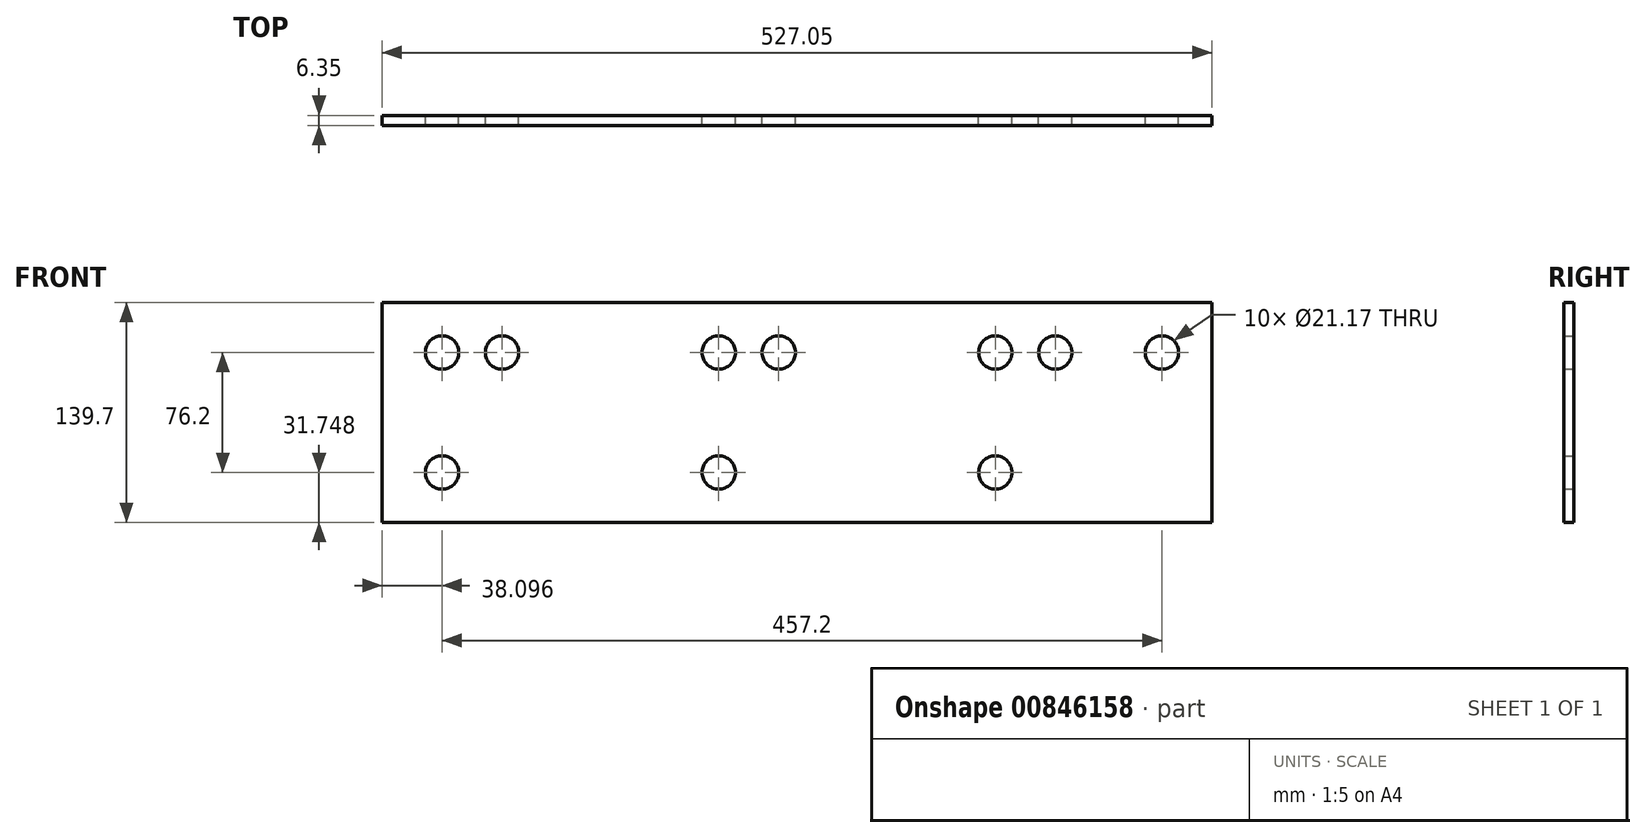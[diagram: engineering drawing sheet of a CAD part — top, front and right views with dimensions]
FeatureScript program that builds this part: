
annotation { "Feature Type Name" : "Feature", "Feature Type Description" : "" }
export const myFeature = defineFeature(function(context is Context, id is Id, definition is map)
    precondition{}
    {
        {
            var Q0;
            Q0=qCreatedBy(makeId("Front.planeOp"),FACE);
            var sketch = newSketch(context, id + "F0", { "sketchPlane" : qUnion([Q0])});
            skLineSegment(sketch, "E0.bottom", {"start": v(-265.63, 28.06) * mm, "end": v(261.42, 28.06) * mm});
            skLineSegment(sketch, "E0.top", {"start": v(-265.63, -111.64) * mm, "end": v(261.42, -111.64) * mm});
            skLineSegment(sketch, "E0.left", {"start": v(-265.63, 28.06) * mm, "end": v(-265.63, -111.64) * mm});
            skLineSegment(sketch, "E0.right", {"start": v(261.42, 28.06) * mm, "end": v(261.42, -111.64) * mm});
            skLineSegment(sketch, "E1", {"start": v(-87.83, 28.06) * mm, "end": v(-87.83, -111.64) * mm});
            skLineSegment(sketch, "E2", {"start": v(89.97, 28.06) * mm, "end": v(89.97, -111.64) * mm});
            skSolve(sketch);
        }
        {
            var Q0;
            {var subQ0=sQuery(id+"F0.wireOp",EDGE,"E0.left");Q0=makeQuery(id+"F0.imprint","IMPRINT",FACE,{"disambiguationData":[TD([[makeQuery(id+"F0.imprint","IMPRINT",EDGE,{"derivedFrom":subQ0}),1.0]])]});}
            var sketch = newSketch(context, id + "F1", { "sketchPlane" : qUnion([Q0])});
            skCircle(sketch, "E3", {"center": v(-189.43, -3.7) * mm, "radius": 10.58 * mm});
            skCircle(sketch, "E4", {"center": v(-227.53, -3.7) * mm, "radius": 10.58 * mm});
            skCircle(sketch, "E5", {"center": v(-227.53, -79.9) * mm, "radius": 10.58 * mm});
            skCircle(sketch, "E6", {"center": v(-51.85, -79.9) * mm, "radius": 10.58 * mm});
            skCircle(sketch, "E7", {"center": v(-51.85, -3.7) * mm, "radius": 10.58 * mm});
            skCircle(sketch, "E8", {"center": v(-13.75, -3.7) * mm, "radius": 10.58 * mm});
            skCircle(sketch, "E9", {"center": v(123.83, -3.7) * mm, "radius": 10.58 * mm});
            skCircle(sketch, "E10", {"center": v(161.93, -3.7) * mm, "radius": 10.58 * mm});
            skCircle(sketch, "E11", {"center": v(123.83, -79.9) * mm, "radius": 10.58 * mm});
            skCircle(sketch, "E12", {"center": v(229.67, -3.7) * mm, "radius": 10.58 * mm});
            skSolve(sketch);
        }
        {
            var Q0;
            {var subQ0=sQuery(id+"F0.wireOp",EDGE,"E0.left");Q0=makeQuery(id+"F0.imprint","IMPRINT",FACE,{"disambiguationData":[TD([[makeQuery(id+"F0.imprint","IMPRINT",EDGE,{"derivedFrom":subQ0}),1.0]])]});}
            var Q1;
            {var subQ0=sQuery(id+"F0.wireOp",EDGE,"E1");Q1=makeQuery(id+"F0.imprint","IMPRINT",FACE,{"disambiguationData":[TD([[makeQuery(id+"F0.imprint","IMPRINT",EDGE,{"derivedFrom":subQ0}),1.0]])]});}
            var Q2;
            {var subQ0=sQuery(id+"F0.wireOp",EDGE,"E0.right");Q2=makeQuery(id+"F0.imprint","IMPRINT",FACE,{"disambiguationData":[TD([[makeQuery(id+"F0.imprint","IMPRINT",EDGE,{"derivedFrom":subQ0}),-1.0]])]});}
            extrude(context, id + "F2", {"entities" : qUnion([Q0, Q1, Q2]), "depth" : 6.35 * mm, "offsetDistance" : 25.4 * mm});
        }
        {
            var Q0;
            Q0=sQuery(id+"F1.wireOp",VERTEX,"E4.center");
            var Q1;
            Q1=sQuery(id+"F1.wireOp",VERTEX,"E3.center");
            var Q2;
            Q2=sQuery(id+"F1.wireOp",VERTEX,"E5.center");
            var Q3;
            Q3=sQuery(id+"F1.wireOp",VERTEX,"E7.center");
            var Q4;
            Q4=sQuery(id+"F1.wireOp",VERTEX,"E8.center");
            var Q5;
            Q5=sQuery(id+"F1.wireOp",VERTEX,"E6.center");
            var Q6;
            Q6=sQuery(id+"F1.wireOp",VERTEX,"E9.center");
            var Q7;
            Q7=sQuery(id+"F1.wireOp",VERTEX,"E10.center");
            var Q8;
            Q8=sQuery(id+"F1.wireOp",VERTEX,"E11.center");
            var Q9;
            Q9=sQuery(id+"F1.wireOp",VERTEX,"E12.center");
            var Q10;
            Q10=makeQuery(id+"F2.opExtrude","SWEPT_BODY",BODY,{"disambiguationData":[OSD([sQuery(id+"F0.wireOp",EDGE,"E0.bottom"),sQuery(id+"F0.wireOp",EDGE,"E0.top"),sQuery(id+"F0.wireOp",EDGE,"E0.left"),sQuery(id+"F0.wireOp",EDGE,"E0.right")])]});
            hole(context, id + "F3", {"style" : HoleStyle.SIMPLE, "endStyle" : HoleEndStyle.BLIND, "oppositeDirection" : true, "holeDiameter" : 21.17 * mm, "majorDiameter" : 6.35 * mm, "holeDepth" : 12.7 * mm, "isTappedThrough" : true, "tappedDepth" : 12.7 * mm, "tapClearance" : 3, "locations" : qUnion([Q0, Q1, Q2, Q3, Q4, Q5, Q6, Q7, Q8, Q9]), "scope" : qUnion([Q10])});
        }
    });
